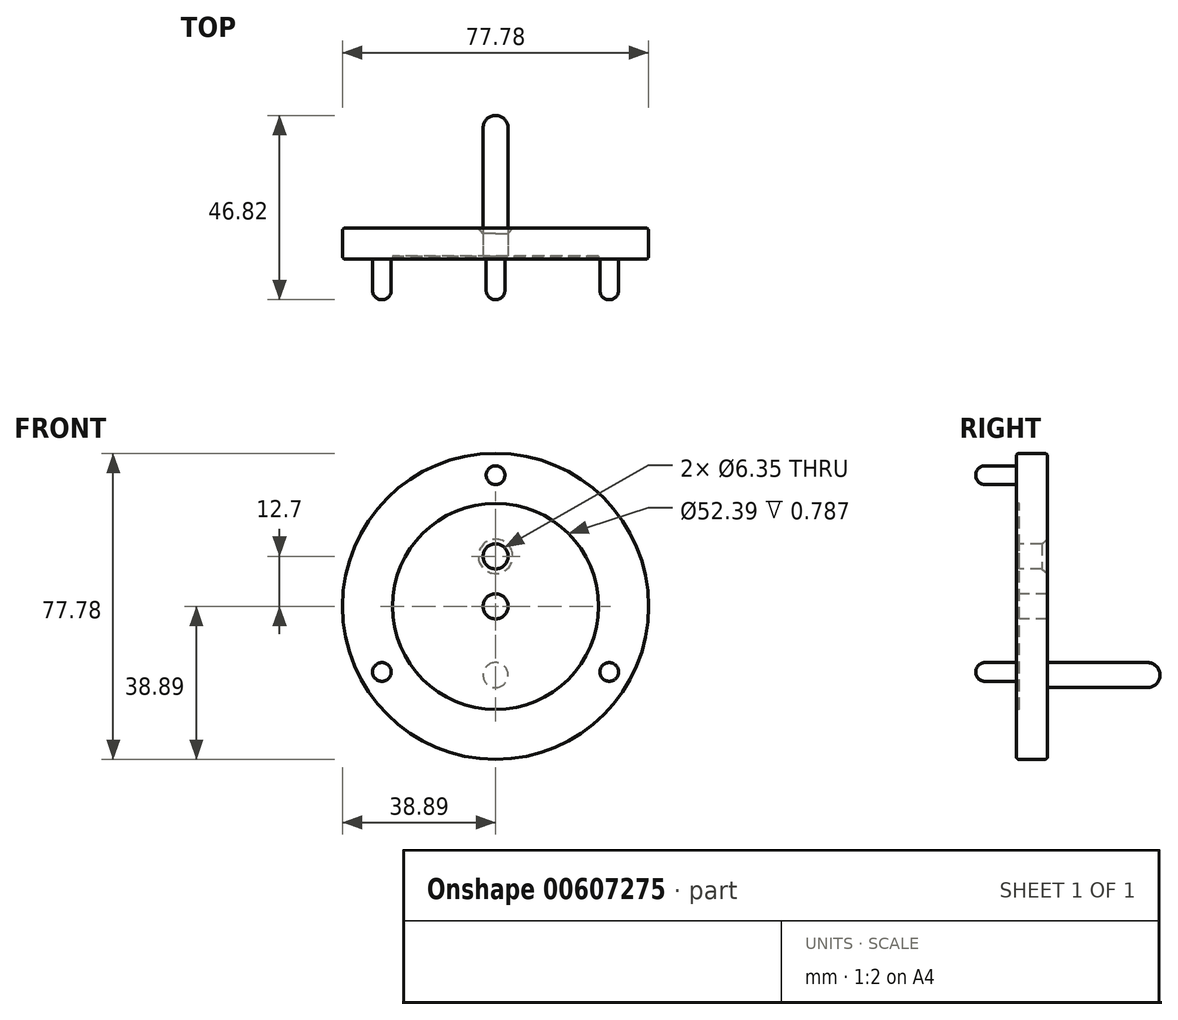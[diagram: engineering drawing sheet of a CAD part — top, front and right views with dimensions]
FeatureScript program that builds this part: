
annotation { "Feature Type Name" : "Feature", "Feature Type Description" : "" }
export const myFeature = defineFeature(function(context is Context, id is Id, definition is map)
    precondition{}
    {
        {
            var Q0;
            Q0=qCreatedBy(makeId("Front.planeOp"),FACE);
            var sketch = newSketch(context, id + "F0", { "sketchPlane" : qUnion([Q0])});
            skCircle(sketch, "E0", {"center": v(0, 0) * mm, "radius": 38.9 * mm});
            skSolve(sketch);
        }
        {
            var Q0;
            Q0 = qSketchRegion(id + "F0", true);
            extrude(context, id + "F1", {"entities" : qUnion([Q0]), "depth" : 7.94 * mm, "offsetDistance" : 25.4 * mm});
        }
        {
            var Q0;
            Q0=makeQuery(id+"F1.opExtrude","CAP_FACE",FACE,{"disambiguationData":[OSD([sQuery(id+"F0.wireOp",EDGE,"E0")])],"isStart":false});
            var sketch = newSketch(context, id + "F2", { "sketchPlane" : qUnion([Q0])});
            skCircle(sketch, "E1", {"center": v(0, 0) * mm, "radius": 26.2 * mm});
            skSolve(sketch);
        }
        {
            var Q0;
            Q0 = qSketchRegion(id + "F2", true);
            extrude(context, id + "F3", {"entities" : qUnion([Q0]), "operationType" : NewBodyOperationType.REMOVE, "oppositeDirection" : true, "depth" : 0.79 * mm, "offsetDistance" : 25.4 * mm});
        }
        {
            var Q0;
            Q0=makeQuery(id+"F1.opExtrude","CAP_FACE",FACE,{"disambiguationData":[OSD([sQuery(id+"F0.wireOp",EDGE,"E0")])],"isStart":false});
            var sketch = newSketch(context, id + "F4", { "sketchPlane" : qUnion([Q0])});
            skLineSegment(sketch, "E2", {"start": v(0, 0) * mm, "end": v(0, 33.34) * mm, "construction": true});
            skCircle(sketch, "E3", {"center": v(0, 33.34) * mm, "radius": 2.38 * mm});
            skPoint(sketch, "E4.center", {"position": v(0, 0) * mm});
            skCircle(sketch, "E5.1.0", {"center": v(-28.87, -16.67) * mm, "radius": 2.38 * mm});
            skCircle(sketch, "E5.2.0", {"center": v(28.87, -16.67) * mm, "radius": 2.38 * mm});
            skSolve(sketch);
        }
        {
            var Q0;
            Q0 = qSketchRegion(id + "F4", true);
            extrude(context, id + "F5", {"entities" : qUnion([Q0]), "operationType" : NewBodyOperationType.ADD, "depth" : 10.3 * mm, "offsetDistance" : 25.4 * mm});
        }
        {
            var Q0;
            Q0=makeQuery(id+"F5.opExtrude","CAP_EDGE",EDGE,{"disambiguationData":[OSD([sQuery(id+"F4.wireOp",EDGE,"E3")])],"isStart":false});
            var Q1;
            Q1=makeQuery(id+"F5.opExtrude","CAP_EDGE",EDGE,{"disambiguationData":[OSD([sQuery(id+"F4.wireOp",EDGE,"E5.2.0")])],"isStart":false});
            var Q2;
            Q2=makeQuery(id+"F5.opExtrude","CAP_EDGE",EDGE,{"disambiguationData":[OSD([sQuery(id+"F4.wireOp",EDGE,"E5.1.0")])],"isStart":false});
            fillet(context, id + "F6", {"entities" : qUnion([Q0, Q1, Q2]), "radius" : 2.38 * mm, "tangentPropagation" : true, "allowEdgeOverflow" : false});
        }
        {
            var Q0;
            Q0=makeQuery(id+"F3.boolean.opBoolean","COPY",FACE,{"derivedFrom":makeQuery(id+"F3.opExtrude","CAP_FACE",FACE,{"disambiguationData":[OSD([sQuery(id+"F2.wireOp",EDGE,"E1")])],"isStart":false})});
            var sketch = newSketch(context, id + "F7", { "sketchPlane" : qUnion([Q0])});
            skCircle(sketch, "E6", {"center": v(0, 0) * mm, "radius": 3.18 * mm});
            skLineSegment(sketch, "E7", {"start": v(0, 0) * mm, "end": v(0, 12.7) * mm, "construction": true});
            skCircle(sketch, "E8", {"center": v(0, 12.7) * mm, "radius": 3.18 * mm});
            skSolve(sketch);
        }
        {
            var Q0;
            Q0=makeQuery(id+"F7.imprint","IMPRINT",FACE,{"disambiguationData":[TD([[makeQuery(id+"F7.imprint","IMPRINT",EDGE,{"derivedFrom":sQuery(id+"F7.wireOp",EDGE,"E6")}),1.0]])]});
            var Q1;
            Q1=makeQuery(id+"F7.imprint","IMPRINT",FACE,{"disambiguationData":[TD([[makeQuery(id+"F7.imprint","IMPRINT",EDGE,{"derivedFrom":sQuery(id+"F7.wireOp",EDGE,"E8")}),1.0]])]});
            extrude(context, id + "F8", {"entities" : qUnion([Q0, Q1]), "operationType" : NewBodyOperationType.REMOVE, "endBound" : BoundingType.THROUGH_ALL, "oppositeDirection" : true, "depth" : 25.4 * mm, "offsetDistance" : 25.4 * mm});
        }
        {
            var Q0;
            Q0=makeQuery(id+"F1.opExtrude","CAP_FACE",FACE,{"disambiguationData":[OSD([sQuery(id+"F0.wireOp",EDGE,"E0")])],"isStart":true});
            var sketch = newSketch(context, id + "F9", { "sketchPlane" : qUnion([Q0])});
            skPoint(sketch, "E9", {"position": v(0, 12.7) * mm});
            skSolve(sketch);
        }
        {
            var Q0;
            Q0=sQuery(id+"F9.wireOp",VERTEX,"E9");
            var Q1;
            Q1=makeQuery(id+"F1.opExtrude","SWEPT_BODY",BODY,{"disambiguationData":[OSD([sQuery(id+"F0.wireOp",EDGE,"E0")])]});
            hole(context, id + "F10", {"style" : HoleStyle.C_SINK, "endStyle" : HoleEndStyle.THROUGH, "holeDiameter" : 6.35 * mm, "cSinkDiameter" : 8.74 * mm, "cSinkAngle" : 82 * degree, "majorDiameter" : 7.94 * mm, "isTappedThrough" : true, "tappedDepth" : 21.59 * mm, "tapClearance" : 20, "locations" : qUnion([Q0]), "scope" : qUnion([Q1])});
        }
        {
            var Q0;
            Q0=makeQuery(id+"F1.opExtrude","CAP_FACE",FACE,{"disambiguationData":[OSD([sQuery(id+"F0.wireOp",EDGE,"E0")])],"isStart":true});
            var sketch = newSketch(context, id + "F11", { "sketchPlane" : qUnion([Q0])});
            skLineSegment(sketch, "E10", {"start": v(0, 0) * mm, "end": v(0, -17.46) * mm, "construction": true});
            skCircle(sketch, "E11", {"center": v(0, -17.46) * mm, "radius": 3.18 * mm});
            skSolve(sketch);
        }
        {
            var Q0;
            Q0=makeQuery(id+"F11.imprint","IMPRINT",FACE,{"disambiguationData":[TD([[makeQuery(id+"F11.imprint","IMPRINT",EDGE,{"derivedFrom":sQuery(id+"F11.wireOp",EDGE,"E11")}),1.0]])]});
            extrude(context, id + "F12", {"entities" : qUnion([Q0]), "operationType" : NewBodyOperationType.ADD, "depth" : 28.57 * mm, "offsetDistance" : 25.4 * mm});
        }
        {
            var Q0;
            Q0=makeQuery(id+"F12.opExtrude","CAP_EDGE",EDGE,{"disambiguationData":[OSD([sQuery(id+"F11.wireOp",EDGE,"E11")])],"isStart":false});
            fillet(context, id + "F13", {"entities" : qUnion([Q0]), "radius" : 3.17 * mm, "tangentPropagation" : true, "allowEdgeOverflow" : false});
        }
        {
            var Q0;
            Q0=makeQuery(id+"F1.opExtrude","CAP_EDGE",EDGE,{"disambiguationData":[OSD([sQuery(id+"F0.wireOp",EDGE,"E0")])],"isStart":false});
            var Q1;
            Q1=makeQuery(id+"F1.opExtrude","CAP_EDGE",EDGE,{"disambiguationData":[OSD([sQuery(id+"F0.wireOp",EDGE,"E0")])],"isStart":true});
            fillet(context, id + "F14", {"entities" : qUnion([Q0, Q1]), "radius" : 0.79 * mm, "tangentPropagation" : true, "allowEdgeOverflow" : false});
        }
    });
